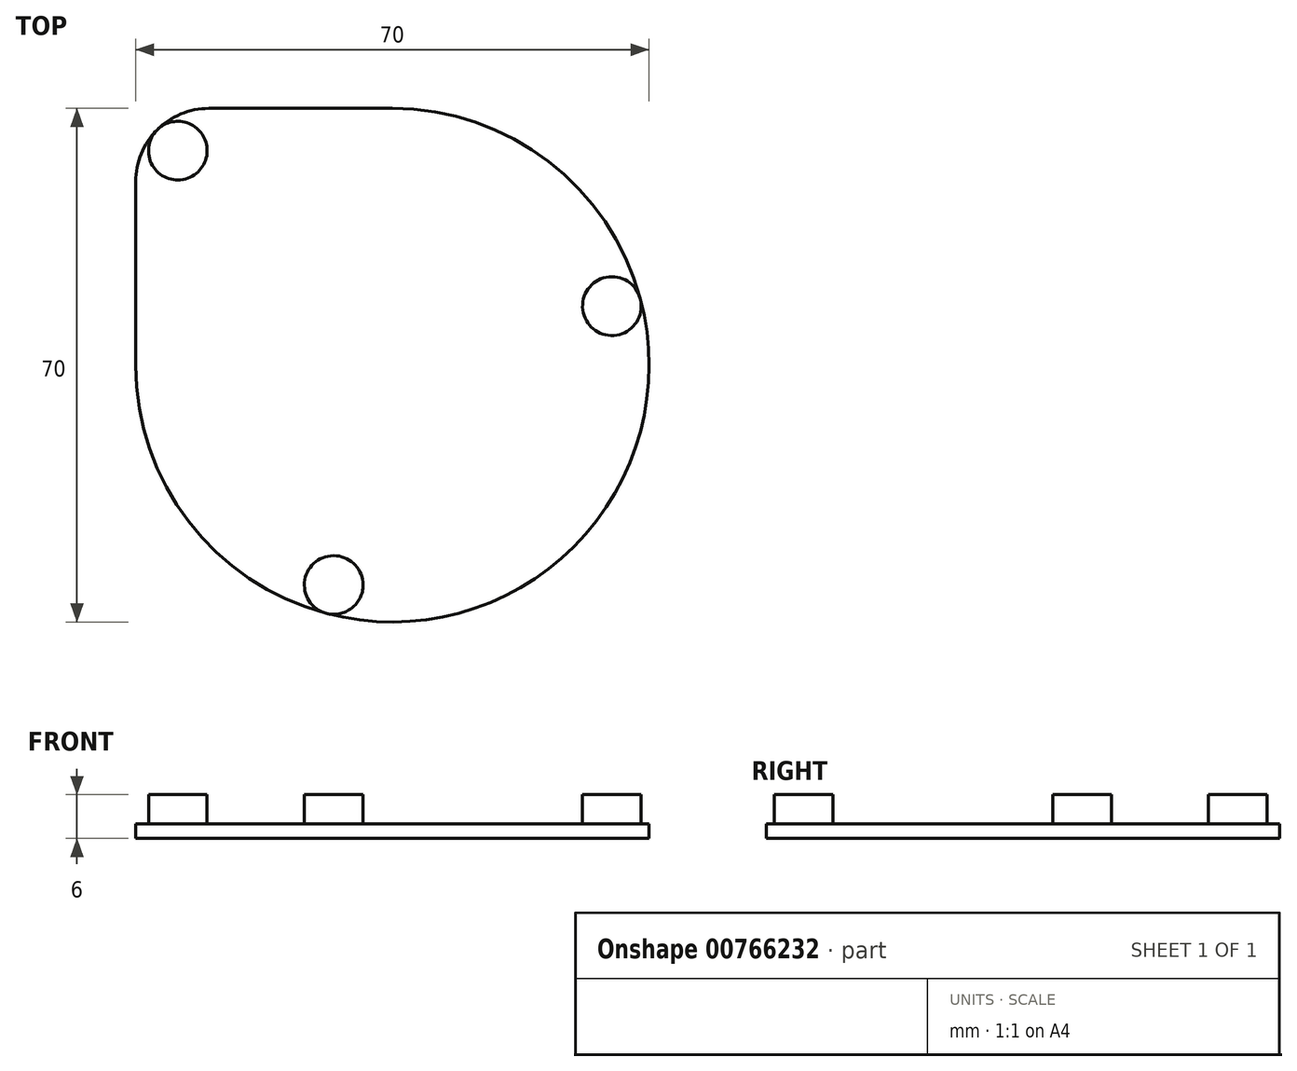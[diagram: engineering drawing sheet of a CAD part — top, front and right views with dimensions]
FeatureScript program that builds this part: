
annotation { "Feature Type Name" : "Feature", "Feature Type Description" : "" }
export const myFeature = defineFeature(function(context is Context, id is Id, definition is map)
    precondition{}
    {
        {
            var Q0;
            Q0=qCreatedBy(makeId("Top.planeOp"),FACE);
            var sketch = newSketch(context, id + "F0", { "sketchPlane" : qUnion([Q0])});
            skCircle(sketch, "E0", {"center": v(0, 0) * mm, "radius": 35 * mm});
            skLineSegment(sketch, "E1.bottom", {"start": v(-35, 0) * mm, "end": v(0, 0) * mm});
            skLineSegment(sketch, "E1.top", {"start": v(-25, 35) * mm, "end": v(0, 35) * mm});
            skLineSegment(sketch, "E1.left", {"start": v(-35, 0) * mm, "end": v(-35, 25) * mm});
            skLineSegment(sketch, "E1.right", {"start": v(0, 0) * mm, "end": v(0, 35) * mm});
            skPoint(sketch, "E2.visualSharp", {"position": v(-35, 35) * mm});
            skArc(sketch, "E2.filletArc", {"start": v(-25, 35) * mm, "mid": v(-32.07, 32.07) * mm, "end": v(-35, 25) * mm});
            skSolve(sketch);
        }
        {
            var Q0;
            Q0 = qSketchRegion(id + "F0", true);
            extrude(context, id + "F1", {"entities" : qUnion([Q0]), "depth" : 2 * mm, "offsetDistance" : 25 * mm});
        }
        {
            var Q0;
            Q0=makeQuery(id+"F1.opExtrude","CAP_FACE",FACE,{"disambiguationData":[OSD([sQuery(id+"F0.wireOp",EDGE,"E0"),sQuery(id+"F0.wireOp",EDGE,"E1.top"),sQuery(id+"F0.wireOp",EDGE,"E1.left"),sQuery(id+"F0.wireOp",EDGE,"E2.filletArc")])],"isStart":false});
            var sketch = newSketch(context, id + "F2", { "sketchPlane" : qUnion([Q0])});
            skArc(sketch, "E3.0", {"start": v(-31, 0) * mm, "mid": v(21.92, -21.92) * mm, "end": v(0, 31) * mm});
            skLineSegment(sketch, "E3.1", {"start": v(-31, 0) * mm, "end": v(-31, 25) * mm, "construction": true});
            skArc(sketch, "E3.2", {"start": v(-25, 31) * mm, "mid": v(-29.24, 29.24) * mm, "end": v(-31, 25) * mm, "construction": true});
            skLineSegment(sketch, "E3.3", {"start": v(-25, 31) * mm, "end": v(0, 31) * mm, "construction": true});
            skCircle(sketch, "E4.cCircle", {"center": v(0, 0) * mm, "radius": 31 * mm, "construction": true});
            skLineSegment(sketch, "E4.0", {"start": v(29.93, 8.06) * mm, "end": v(-8, -29.95) * mm, "construction": true});
            skLineSegment(sketch, "E4.1", {"start": v(-8, -29.95) * mm, "end": v(-21.94, 21.9) * mm, "construction": true});
            skLineSegment(sketch, "E4.2", {"start": v(-21.94, 21.9) * mm, "end": v(29.93, 8.06) * mm, "construction": true});
            skCircle(sketch, "E5", {"center": v(-8, -29.95) * mm, "radius": 4 * mm});
            skCircle(sketch, "E6", {"center": v(29.93, 8.06) * mm, "radius": 4 * mm});
            skCircle(sketch, "E7", {"center": v(-29.24, 29.24) * mm, "radius": 4 * mm});
            skLineSegment(sketch, "E8", {"start": v(-32.07, 32.07) * mm, "end": v(-21.92, 21.92) * mm, "construction": true});
            skSolve(sketch);
        }
        {
            var Q0;
            Q0 = qSketchRegion(id + "F2", true);
            extrude(context, id + "F3", {"entities" : qUnion([Q0]), "operationType" : NewBodyOperationType.ADD, "depth" : 4 * mm, "offsetDistance" : 25 * mm});
        }
    });
